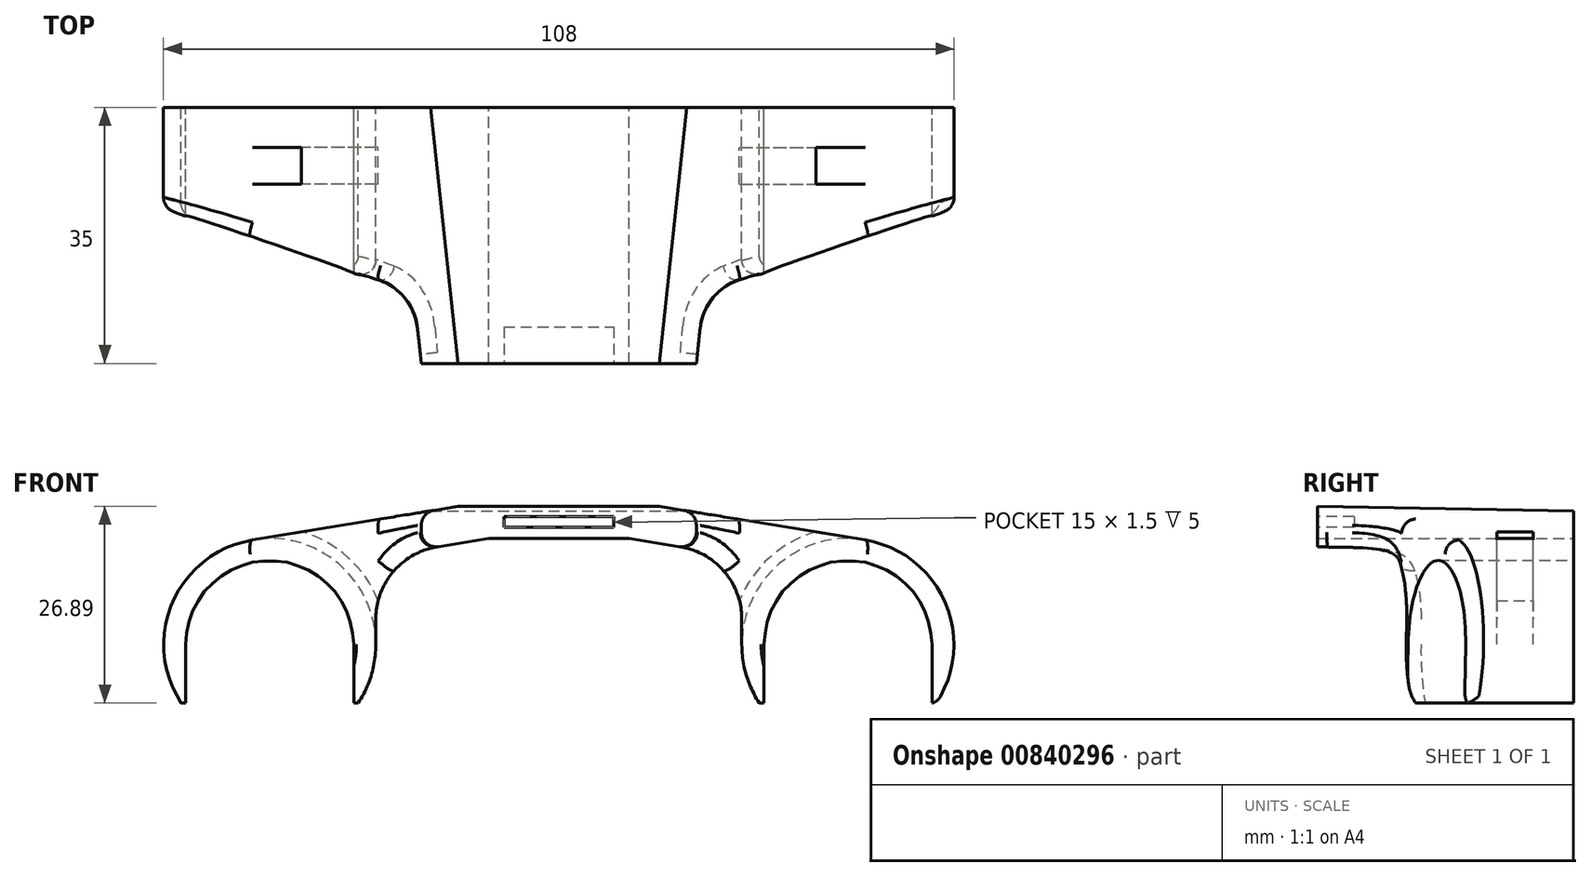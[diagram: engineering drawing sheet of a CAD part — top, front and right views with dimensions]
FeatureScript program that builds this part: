
annotation { "Feature Type Name" : "Feature", "Feature Type Description" : "" }
export const myFeature = defineFeature(function(context is Context, id is Id, definition is map)
    precondition{}
    {
        {
            var Q0;
            Q0=qCreatedBy(makeId("Front.planeOp"),FACE);
            var sketch = newSketch(context, id + "F0", { "sketchPlane" : qUnion([Q0])});
            skArc(sketch, "E0", {"start": v(51, 0) * mm, "mid": v(39.5, 11.5) * mm, "end": v(28, 0) * mm});
            skLineSegment(sketch, "E1", {"start": v(0, 0) * mm, "end": v(39.5, 0) * mm, "construction": true});
            skArc(sketch, "E2.0", {"start": v(51.6, -8) * mm, "mid": v(52.78, 5.81) * mm, "end": v(41.83, 14.31) * mm});
            skLineSegment(sketch, "E3", {"start": v(0, 19.5) * mm, "end": v(10, 19.5) * mm});
            skLineSegment(sketch, "E4", {"start": v(10, 19.5) * mm, "end": v(41.83, 14.31) * mm});
            skLineSegment(sketch, "E5.0", {"start": v(9.6, 14.5) * mm, "end": v(16.6, 13.36) * mm});
            skLineSegment(sketch, "E5.1", {"start": v(0, 14.5) * mm, "end": v(9.6, 14.5) * mm});
            skLineSegment(sketch, "E6", {"start": v(25, 0) * mm, "end": v(25, 3.49) * mm});
            skPoint(sketch, "E7.visualSharp", {"position": v(25, 11.99) * mm});
            skArc(sketch, "E7.filletArc", {"start": v(25, 3.49) * mm, "mid": v(22.62, 9.96) * mm, "end": v(16.6, 13.36) * mm});
            skLineSegment(sketch, "E8", {"start": v(27.4, -8) * mm, "end": v(28, -8) * mm});
            skLineSegment(sketch, "E9", {"start": v(28, 0) * mm, "end": v(28, -8) * mm});
            skLineSegment(sketch, "E10", {"start": v(51, 0) * mm, "end": v(51, -8) * mm});
            skLineSegment(sketch, "E11.trimOffspring", {"start": v(51, -8) * mm, "end": v(51.6, -8) * mm});
            skArc(sketch, "E12.trimOffspring", {"start": v(25, 0) * mm, "mid": v(25.61, -4.18) * mm, "end": v(27.4, -8) * mm});
            skLineSegment(sketch, "E13", {"start": v(0, 19.5) * mm, "end": v(0, 14.5) * mm});
            skSolve(sketch);
        }
        {
            var Q0;
            Q0=qSketchRegion(id+"F0",true);
            extrude(context, id + "F1", {"entities" : qUnion([Q0]), "endBound" : BoundingType.SYMMETRIC, "depth" : 70 * mm, "offsetDistance" : 25 * mm});
        }
        {
            var Q0;
            Q0=makeQuery(id+"F1.opExtrude","CAP_EDGE",EDGE,{"disambiguationData":[OSD([sQuery(id+"F0.wireOp",EDGE,"E3")])],"isStart":true});
            chamfer(context, id + "F2", {"entities" : qUnion([Q0]), "chamferType" : ChamferType.OFFSET_ANGLE, "width" : 70 * mm, "oppositeDirection" : true, "angle" : 1 * degree, "tangentPropagation" : true});
        }
        {
            var Q0;
            Q0=makeQuery(id+"F2.opChamfer","BLEND_FACE",FACE,{"disambiguationData":[OSD([sQuery(id+"F0.wireOp",EDGE,"E3")])]});
            var sketch = newSketch(context, id + "F3", { "sketchPlane" : qUnion([Q0])});
            skLineSegment(sketch, "E14", {"start": v(55, 21.6) * mm, "end": v(19.84, 9.57) * mm});
            skLineSegment(sketch, "E15", {"start": v(17.7, -10.33) * mm, "end": v(55, -21.1) * mm});
            skLineSegment(sketch, "E16", {"start": v(55, -21.1) * mm, "end": v(55, 21.6) * mm});
            skLineSegment(sketch, "E17", {"start": v(17.7, -10.33) * mm, "end": v(19.84, 9.57) * mm});
            skPoint(sketch, "E18.orphan", {"position": v(16.1, 8.29) * mm});
            skSolve(sketch);
        }
        {
            var Q0;
            Q0=makeQuery(id+"F3.imprint","IMPRINT",FACE,{"disambiguationData":[TD([[makeQuery(id+"F3.imprint","IMPRINT",EDGE,{"derivedFrom":sQuery(id+"F3.wireOp",EDGE,"E14")}),1.0]])]});
            extrude(context, id + "F4", {"entities" : qUnion([Q0]), "operationType" : NewBodyOperationType.REMOVE, "endBound" : BoundingType.THROUGH_ALL, "oppositeDirection" : true, "depth" : 25 * mm, "offsetDistance" : 25 * mm});
        }
        {
            var Q0;
            Q0=makeQuery(id+"F4.boolean.opBoolean","COPY",EDGE,{"derivedFrom":makeQuery(id+"F4.opExtrude","SWEPT_EDGE",EDGE,{"disambiguationData":[OSD([sQuery(id+"F3.wireOp",EDGE,"E14"),sQuery(id+"F3.wireOp",EDGE,"E17")])]})});
            var Q1;
            Q1=makeQuery(id+"F4.boolean.opBoolean","COPY",EDGE,{"derivedFrom":makeQuery(id+"F4.opExtrude","SWEPT_EDGE",EDGE,{"disambiguationData":[OSD([sQuery(id+"F3.wireOp",EDGE,"E15"),sQuery(id+"F3.wireOp",EDGE,"E17")])]})});
            fillet(context, id + "F5", {"entities" : qUnion([Q0, Q1]), "radius" : 8 * mm, "tangentPropagation" : true, "allowEdgeOverflow" : false});
        }
        {
            var Q0;
            {var subQ0=makeQuery(id+"F1.opExtrude","CAP_FACE",FACE,{"disambiguationData":[OSD([sQuery(id+"F0.wireOp",EDGE,"E0"),sQuery(id+"F0.wireOp",EDGE,"E2.0"),sQuery(id+"F0.wireOp",EDGE,"E3"),sQuery(id+"F0.wireOp",EDGE,"E4"),sQuery(id+"F0.wireOp",EDGE,"E5.0"),sQuery(id+"F0.wireOp",EDGE,"E5.1"),sQuery(id+"F0.wireOp",EDGE,"E6"),sQuery(id+"F0.wireOp",EDGE,"E7.filletArc"),sQuery(id+"F0.wireOp",EDGE,"E8"),sQuery(id+"F0.wireOp",EDGE,"E9"),sQuery(id+"F0.wireOp",EDGE,"E10"),sQuery(id+"F0.wireOp",EDGE,"E11.trimOffspring"),sQuery(id+"F0.wireOp",EDGE,"E12.trimOffspring"),sQuery(id+"F0.wireOp",EDGE,"E13")])],"isStart":false});Q0=makeQuery(id+"FHFeFmnZixUwJ2z_1.boolean.opBoolean","MERGE",FACE,{"derivedFrom":[subQ0,makeQuery(id+"FHFeFmnZixUwJ2z_1.opPattern","COPY",FACE,{"derivedFrom":subQ0,"instanceName":"1"})]});}
            cPlane(context, id + "F6", {"entities" : qUnion([Q0]), "cplaneType" : CPlaneType.OFFSET, "offset" : 8 * mm, "oppositeDirection" : true, "width" : 150 * mm, "height" : 150 * mm});
        }
        {
            var Q0;
            {var subQ0=makeQuery(id+"F1.opExtrude","CAP_FACE",FACE,{"disambiguationData":[OSD([sQuery(id+"F0.wireOp",EDGE,"E0"),sQuery(id+"F0.wireOp",EDGE,"E2.0"),sQuery(id+"F0.wireOp",EDGE,"E3"),sQuery(id+"F0.wireOp",EDGE,"E4"),sQuery(id+"F0.wireOp",EDGE,"E5.0"),sQuery(id+"F0.wireOp",EDGE,"E5.1"),sQuery(id+"F0.wireOp",EDGE,"E6"),sQuery(id+"F0.wireOp",EDGE,"E7.filletArc"),sQuery(id+"F0.wireOp",EDGE,"E8"),sQuery(id+"F0.wireOp",EDGE,"E9"),sQuery(id+"F0.wireOp",EDGE,"E10"),sQuery(id+"F0.wireOp",EDGE,"E11.trimOffspring"),sQuery(id+"F0.wireOp",EDGE,"E12.trimOffspring"),sQuery(id+"F0.wireOp",EDGE,"E13")])],"isStart":true});Q0=makeQuery(id+"FHFeFmnZixUwJ2z_1.boolean.opBoolean","MERGE",FACE,{"derivedFrom":[subQ0,makeQuery(id+"FHFeFmnZixUwJ2z_1.opPattern","COPY",FACE,{"derivedFrom":subQ0,"instanceName":"1"})]});}
            cPlane(context, id + "F7", {"entities" : qUnion([Q0]), "cplaneType" : CPlaneType.OFFSET, "offset" : 8 * mm, "oppositeDirection" : true, "width" : 150 * mm, "height" : 150 * mm});
        }
        {
            var Q0;
            Q0=qCreatedBy(id+"F6.planeOp",FACE);
            var sketch = newSketch(context, id + "F8", { "sketchPlane" : qUnion([Q0])});
            skArc(sketch, "E19.converted", {"start": v(41.83, 14.31) * mm, "mid": v(30.1, 11.05) * mm, "end": v(25, 0) * mm});
            skPoint(sketch, "E20.orphan", {"position": v(41.83, 14.31) * mm});
            skArc(sketch, "E21.0", {"start": v(35.16, 15.4) * mm, "mid": v(28.83, 11.92) * mm, "end": v(24.67, 6.02) * mm});
            skArc(sketch, "E22.0", {"start": v(25, 3.49) * mm, "mid": v(24.92, 4.76) * mm, "end": v(24.67, 6.02) * mm});
            skLineSegment(sketch, "E23.0", {"start": v(25, 0) * mm, "end": v(25, 3.49) * mm});
            skLineSegment(sketch, "E24.0", {"start": v(35.16, 15.4) * mm, "end": v(41.83, 14.31) * mm});
            skPoint(sketch, "E25.orphan", {"position": v(16.6, 13.36) * mm});
            skPoint(sketch, "E26.orphan", {"position": v(10, 19.5) * mm});
            skSolve(sketch);
        }
        {
            var Q0;
            Q0=qSketchRegion(id+"F8",true);
            extrude(context, id + "F9", {"entities" : qUnion([Q0]), "operationType" : NewBodyOperationType.REMOVE, "endBound" : BoundingType.SYMMETRIC, "oppositeDirection" : true, "depth" : 5 * mm, "offsetDistance" : 25 * mm});
        }
        {
            var Q0;
            Q0=qCreatedBy(id+"F7.planeOp",FACE);
            var sketch = newSketch(context, id + "F10", { "sketchPlane" : qUnion([Q0])});
            skArc(sketch, "E27.converted", {"start": v(-41.83, 14.31) * mm, "mid": v(-30.1, 11.05) * mm, "end": v(-25, 0) * mm});
            skPoint(sketch, "E28.orphan", {"position": v(-41.83, 14.31) * mm});
            skLineSegment(sketch, "E29.0", {"start": v(-35.16, 15.4) * mm, "end": v(-41.83, 14.31) * mm});
            skLineSegment(sketch, "E30.0", {"start": v(-25, 0) * mm, "end": v(-25, 3.49) * mm});
            skArc(sketch, "E31.0", {"start": v(-25, 3.49) * mm, "mid": v(-24.92, 4.76) * mm, "end": v(-24.67, 6.02) * mm});
            skArc(sketch, "E32.0", {"start": v(-35.16, 15.4) * mm, "mid": v(-28.83, 11.92) * mm, "end": v(-24.67, 6.02) * mm});
            skPoint(sketch, "E33.orphan", {"position": v(-17.5, 18.28) * mm});
            skPoint(sketch, "E34.orphan", {"position": v(-16.6, 13.36) * mm});
            skSolve(sketch);
        }
        {
            var Q0;
            Q0=qSketchRegion(id+"F10",true);
            extrude(context, id + "F11", {"entities" : qUnion([Q0]), "operationType" : NewBodyOperationType.REMOVE, "endBound" : BoundingType.SYMMETRIC, "oppositeDirection" : true, "depth" : 5 * mm, "offsetDistance" : 25 * mm});
        }
        {
            var Q0;
            Q0=makeQuery(id+"F1.opExtrude","SWEPT_BODY",BODY,{"disambiguationData":[OSD([sQuery(id+"F0.wireOp",EDGE,"E0"),sQuery(id+"F0.wireOp",EDGE,"E2.0"),sQuery(id+"F0.wireOp",EDGE,"E3"),sQuery(id+"F0.wireOp",EDGE,"E4"),sQuery(id+"F0.wireOp",EDGE,"E5.0"),sQuery(id+"F0.wireOp",EDGE,"E5.1"),sQuery(id+"F0.wireOp",EDGE,"E6"),sQuery(id+"F0.wireOp",EDGE,"E7.filletArc"),sQuery(id+"F0.wireOp",EDGE,"E8"),sQuery(id+"F0.wireOp",EDGE,"E9"),sQuery(id+"F0.wireOp",EDGE,"E10"),sQuery(id+"F0.wireOp",EDGE,"E11.trimOffspring"),sQuery(id+"F0.wireOp",EDGE,"E12.trimOffspring"),sQuery(id+"F0.wireOp",EDGE,"E13")])]});
            var Q1;
            Q1=makeQuery(id+"F1.opExtrude","SWEPT_FACE",FACE,{"disambiguationData":[OSD([sQuery(id+"F0.wireOp",EDGE,"E13")])]});
            mirror(context, id + "F12", {"operationType" : NewBodyOperationType.ADD, "entities" : qUnion([Q0]), "mirrorPlane" : qUnion([Q1])});
        }
        {
            var Q0;
            Q0=makeQuery(id+"F4.boolean.opBoolean","INTERSECT",EDGE,{"derivedFrom":[makeQuery(id+"F1.opExtrude","SWEPT_FACE",FACE,{"disambiguationData":[OSD([sQuery(id+"F0.wireOp",EDGE,"E4")])]}),makeQuery(id+"F4.opExtrude","SWEPT_FACE",FACE,{"disambiguationData":[OSD([sQuery(id+"F3.wireOp",EDGE,"E17")])]})]});
            var Q1;
            Q1=makeQuery(id+"F12.opPattern","COPY",EDGE,{"derivedFrom":makeQuery(id+"F4.boolean.opBoolean","INTERSECT",EDGE,{"derivedFrom":[makeQuery(id+"F1.opExtrude","SWEPT_FACE",FACE,{"disambiguationData":[OSD([sQuery(id+"F0.wireOp",EDGE,"E4")])]}),makeQuery(id+"F4.opExtrude","SWEPT_FACE",FACE,{"disambiguationData":[OSD([sQuery(id+"F3.wireOp",EDGE,"E17")])]})]}),"instanceName":"1"});
            var Q2;
            {var subQ0=sQuery(id+"F0.wireOp",EDGE,"E11.trimOffspring");var subQ1=sQuery(id+"F0.wireOp",EDGE,"E2.0");Q2=makeQuery(id+"F4.boolean.opBoolean","SPLIT",EDGE,{"disambiguationData":[TD([makeQuery(id+"F4.opExtrude","SWEPT_FACE",FACE,{"disambiguationData":[OSD([sQuery(id+"F3.wireOp",EDGE,"E15")])]})])],"derivedFrom":makeQuery(id+"F1.opExtrude","SWEPT_EDGE",EDGE,{"disambiguationData":[OSD([subQ1,subQ0])]})});}
            var Q3;
            {var subQ0=sQuery(id+"F0.wireOp",EDGE,"E11.trimOffspring");var subQ1=sQuery(id+"F0.wireOp",EDGE,"E2.0");Q3=makeQuery(id+"F4.boolean.opBoolean","SPLIT",EDGE,{"disambiguationData":[TD([makeQuery(id+"F4.opExtrude","SWEPT_FACE",FACE,{"disambiguationData":[OSD([sQuery(id+"F3.wireOp",EDGE,"E14")])]})])],"derivedFrom":makeQuery(id+"F1.opExtrude","SWEPT_EDGE",EDGE,{"disambiguationData":[OSD([subQ1,subQ0])]})});}
            var Q4;
            Q4=makeQuery(id+"F4.boolean.opBoolean","INTERSECT",EDGE,{"derivedFrom":[makeQuery(id+"F1.opExtrude","SWEPT_FACE",FACE,{"disambiguationData":[OSD([sQuery(id+"F0.wireOp",EDGE,"E7.filletArc")])]}),makeQuery(id+"F4.opExtrude","SWEPT_FACE",FACE,{"disambiguationData":[OSD([sQuery(id+"F3.wireOp",EDGE,"E17")])]})]});
            var Q5;
            Q5=makeQuery(id+"F4.boolean.opBoolean","INTERSECT",EDGE,{"derivedFrom":[makeQuery(id+"F1.opExtrude","SWEPT_FACE",FACE,{"disambiguationData":[OSD([sQuery(id+"F0.wireOp",EDGE,"E12.trimOffspring")])]}),makeQuery(id+"F4.opExtrude","SWEPT_FACE",FACE,{"disambiguationData":[OSD([sQuery(id+"F3.wireOp",EDGE,"E14")])]})]});
            var Q6;
            Q6=makeQuery(id+"F4.boolean.opBoolean","INTERSECT",EDGE,{"derivedFrom":[makeQuery(id+"F1.opExtrude","SWEPT_FACE",FACE,{"disambiguationData":[OSD([sQuery(id+"F0.wireOp",EDGE,"E6")])]}),makeQuery(id+"F4.opExtrude","SWEPT_FACE",FACE,{"disambiguationData":[OSD([sQuery(id+"F3.wireOp",EDGE,"E14")])]})]});
            var Q7;
            Q7=makeQuery(id+"F4.boolean.opBoolean","INTERSECT",EDGE,{"derivedFrom":[makeQuery(id+"F1.opExtrude","SWEPT_FACE",FACE,{"disambiguationData":[OSD([sQuery(id+"F0.wireOp",EDGE,"E7.filletArc")])]}),makeQuery(id+"F4.opExtrude","SWEPT_FACE",FACE,{"disambiguationData":[OSD([sQuery(id+"F3.wireOp",EDGE,"E14")])]})]});
            var Q8;
            Q8=makeQuery(id+"F5.opFillet","BLEND_EDGE",EDGE,{"blendedFrom":[makeQuery(id+"F4.boolean.opBoolean","COPY",EDGE,{"derivedFrom":makeQuery(id+"F4.opExtrude","SWEPT_EDGE",EDGE,{"disambiguationData":[OSD([sQuery(id+"F3.wireOp",EDGE,"E14"),sQuery(id+"F3.wireOp",EDGE,"E17")])]})}),makeQuery(id+"F1.opExtrude","SWEPT_FACE",FACE,{"disambiguationData":[OSD([sQuery(id+"F0.wireOp",EDGE,"E7.filletArc")])]})],"blendedInto":[makeQuery(id+"F1.opExtrude","SWEPT_FACE",FACE,{"disambiguationData":[OSD([sQuery(id+"F0.wireOp",EDGE,"E7.filletArc")])]})]});
            var Q9;
            Q9=makeQuery(id+"F5.opFillet","BLEND_EDGE",EDGE,{"blendedFrom":[makeQuery(id+"F4.boolean.opBoolean","COPY",EDGE,{"derivedFrom":makeQuery(id+"F4.opExtrude","SWEPT_EDGE",EDGE,{"disambiguationData":[OSD([sQuery(id+"F3.wireOp",EDGE,"E15"),sQuery(id+"F3.wireOp",EDGE,"E17")])]})}),makeQuery(id+"F1.opExtrude","SWEPT_FACE",FACE,{"disambiguationData":[OSD([sQuery(id+"F0.wireOp",EDGE,"E7.filletArc")])]})],"blendedInto":[makeQuery(id+"F1.opExtrude","SWEPT_FACE",FACE,{"disambiguationData":[OSD([sQuery(id+"F0.wireOp",EDGE,"E7.filletArc")])]})]});
            var Q10;
            Q10=makeQuery(id+"F4.boolean.opBoolean","INTERSECT",EDGE,{"derivedFrom":[makeQuery(id+"F1.opExtrude","SWEPT_FACE",FACE,{"disambiguationData":[OSD([sQuery(id+"F0.wireOp",EDGE,"E7.filletArc")])]}),makeQuery(id+"F4.opExtrude","SWEPT_FACE",FACE,{"disambiguationData":[OSD([sQuery(id+"F3.wireOp",EDGE,"E15")])]})]});
            var Q11;
            Q11=makeQuery(id+"F4.boolean.opBoolean","INTERSECT",EDGE,{"derivedFrom":[makeQuery(id+"F1.opExtrude","SWEPT_FACE",FACE,{"disambiguationData":[OSD([sQuery(id+"F0.wireOp",EDGE,"E6")])]}),makeQuery(id+"F4.opExtrude","SWEPT_FACE",FACE,{"disambiguationData":[OSD([sQuery(id+"F3.wireOp",EDGE,"E15")])]})]});
            var Q12;
            Q12=makeQuery(id+"F4.boolean.opBoolean","INTERSECT",EDGE,{"derivedFrom":[makeQuery(id+"F1.opExtrude","SWEPT_FACE",FACE,{"disambiguationData":[OSD([sQuery(id+"F0.wireOp",EDGE,"E12.trimOffspring")])]}),makeQuery(id+"F4.opExtrude","SWEPT_FACE",FACE,{"disambiguationData":[OSD([sQuery(id+"F3.wireOp",EDGE,"E15")])]})]});
            var Q13;
            Q13=makeQuery(id+"F12.opPattern","COPY",EDGE,{"derivedFrom":makeQuery(id+"F4.boolean.opBoolean","INTERSECT",EDGE,{"derivedFrom":[makeQuery(id+"F1.opExtrude","SWEPT_FACE",FACE,{"disambiguationData":[OSD([sQuery(id+"F0.wireOp",EDGE,"E7.filletArc")])]}),makeQuery(id+"F4.opExtrude","SWEPT_FACE",FACE,{"disambiguationData":[OSD([sQuery(id+"F3.wireOp",EDGE,"E17")])]})]}),"instanceName":"1"});
            fillet(context, id + "F13", {"entities" : qUnion([Q0, Q1, Q2, Q3, Q4, Q5, Q6, Q7, Q8, Q9, Q10, Q11, Q12, Q13]), "radius" : 2 * mm, "tangentPropagation" : true, "allowEdgeOverflow" : false});
        }
        {
            var Q0;
            Q0=qCreatedBy(makeId("Top.planeOp"),FACE);
            var sketch = newSketch(context, id + "F14", { "sketchPlane" : qUnion([Q0])});
            skLineSegment(sketch, "E35.bottom", {"start": v(-70, -40) * mm, "end": v(70, -40) * mm});
            skLineSegment(sketch, "E35.top", {"start": v(-70, 0) * mm, "end": v(70, 0) * mm});
            skLineSegment(sketch, "E35.left", {"start": v(-70, -40) * mm, "end": v(-70, 0) * mm});
            skLineSegment(sketch, "E35.right", {"start": v(70, -40) * mm, "end": v(70, 0) * mm});
            skSolve(sketch);
        }
        {
            var Q0;
            Q0=makeQuery(id+"F14.imprint","IMPRINT",FACE,{"disambiguationData":[TD([[makeQuery(id+"F14.imprint","IMPRINT",EDGE,{"derivedFrom":sQuery(id+"F14.wireOp",EDGE,"E35.bottom")}),1.0]])]});
            extrude(context, id + "F15", {"entities" : qUnion([Q0]), "operationType" : NewBodyOperationType.REMOVE, "endBound" : BoundingType.SYMMETRIC, "oppositeDirection" : true, "depth" : 40 * mm, "offsetDistance" : 25 * mm});
        }
        {
            var Q0;
            Q0=makeQuery(id+"F15.boolean.opBoolean","COPY",FACE,{"derivedFrom":makeQuery(id+"F15.opExtrude","SWEPT_FACE",FACE,{"disambiguationData":[OSD([sQuery(id+"F14.wireOp",EDGE,"E35.top")])]})});
            var sketch = newSketch(context, id + "F16", { "sketchPlane" : qUnion([Q0])});
            skLineSegment(sketch, "E36.bottom", {"start": v(-7.5, 17.5) * mm, "end": v(7.5, 17.5) * mm});
            skLineSegment(sketch, "E36.top", {"start": v(-7.5, 16) * mm, "end": v(7.5, 16) * mm});
            skLineSegment(sketch, "E36.left", {"start": v(-7.5, 17.5) * mm, "end": v(-7.5, 16) * mm});
            skLineSegment(sketch, "E36.right", {"start": v(7.5, 17.5) * mm, "end": v(7.5, 16) * mm});
            skSolve(sketch);
        }
        {
            var Q0;
            Q0=makeQuery(id+"F16.imprint","IMPRINT",FACE,{"disambiguationData":[TD([[makeQuery(id+"F16.imprint","IMPRINT",EDGE,{"derivedFrom":sQuery(id+"F16.wireOp",EDGE,"E36.bottom")}),-1.0]])]});
            extrude(context, id + "F17", {"entities" : qUnion([Q0]), "operationType" : NewBodyOperationType.REMOVE, "oppositeDirection" : true, "depth" : 5 * mm, "offsetDistance" : 25 * mm});
        }
    });
